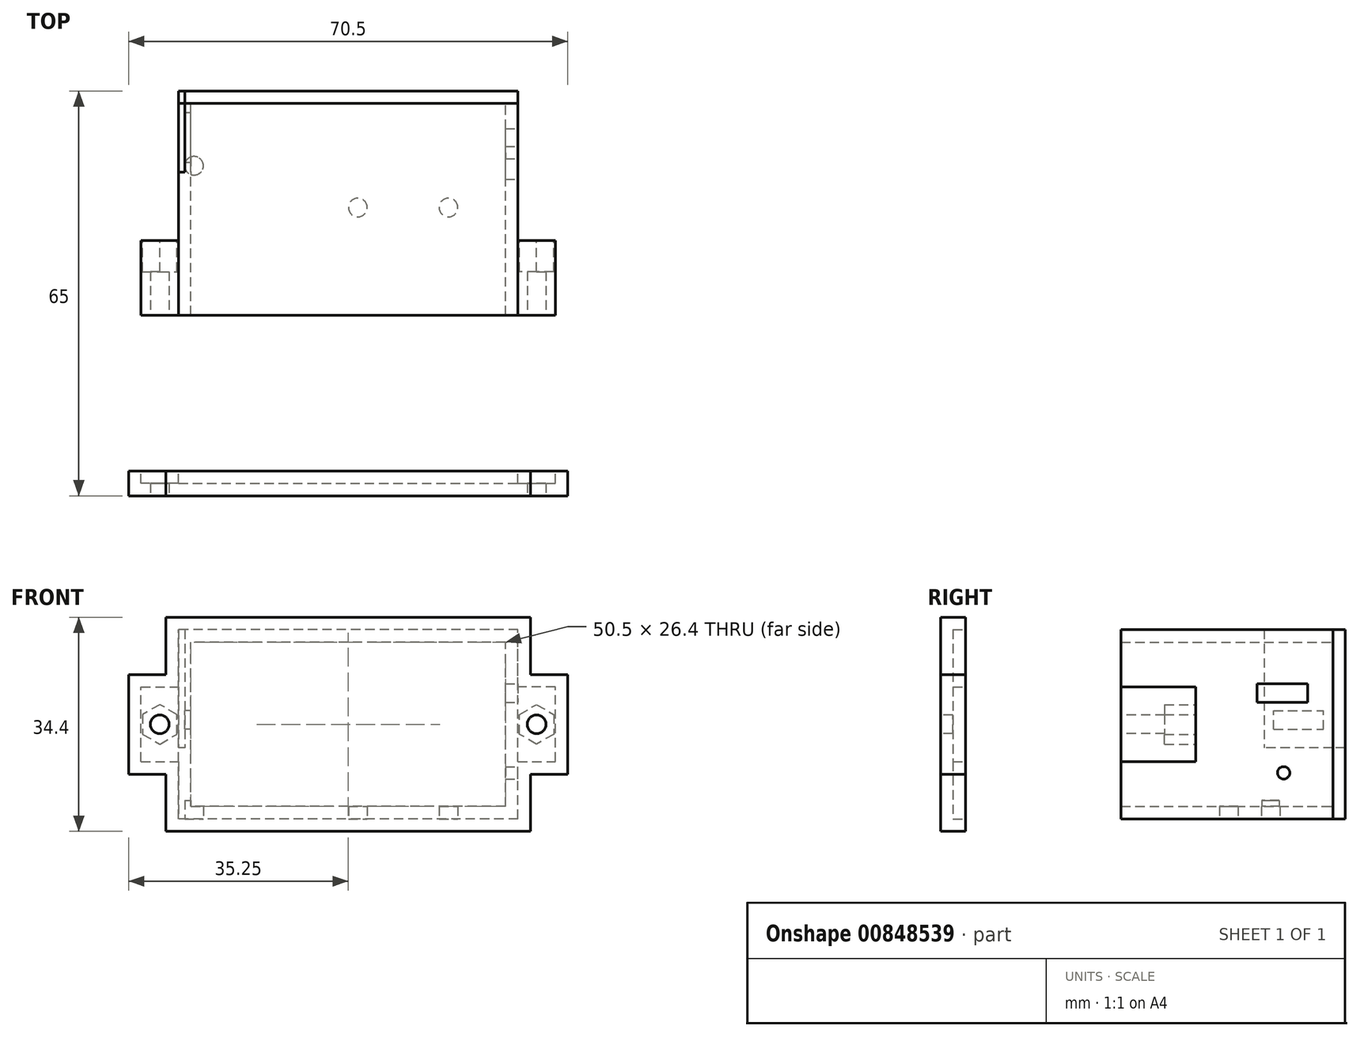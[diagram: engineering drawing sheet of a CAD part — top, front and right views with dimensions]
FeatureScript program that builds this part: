
annotation { "Feature Type Name" : "Feature", "Feature Type Description" : "" }
export const myFeature = defineFeature(function(context is Context, id is Id, definition is map)
    precondition{}
    {
        {
            var Q0;
            Q0=qCreatedBy(makeId("Front.planeOp"),FACE);
            var sketch = newSketch(context, id + "F0", { "sketchPlane" : qUnion([Q0])});
            skLineSegment(sketch, "E0.bottom", {"start": v(27.25, -15.2) * mm, "end": v(-27.25, -15.2) * mm});
            skLineSegment(sketch, "E0.top", {"start": v(27.25, 15.2) * mm, "end": v(-27.25, 15.2) * mm});
            skLineSegment(sketch, "E0.left", {"start": v(27.25, -15.2) * mm, "end": v(27.25, 15.2) * mm});
            skLineSegment(sketch, "E0.right", {"start": v(-27.25, -15.2) * mm, "end": v(-27.25, 15.2) * mm});
            skPoint(sketch, "E0.middle", {"position": v(0, 0) * mm});
            skLineSegment(sketch, "E1.bottom", {"start": v(25.25, -13.2) * mm, "end": v(-25.25, -13.2) * mm});
            skLineSegment(sketch, "E1.top", {"start": v(25.25, 13.2) * mm, "end": v(-25.25, 13.2) * mm});
            skLineSegment(sketch, "E1.left", {"start": v(25.25, -13.2) * mm, "end": v(25.25, 13.2) * mm});
            skLineSegment(sketch, "E1.right", {"start": v(-25.25, -13.2) * mm, "end": v(-25.25, 13.2) * mm});
            skSolve(sketch);
        }
        {
            var Q0;
            Q0=qSketchRegion(id+"F0",true);
            extrude(context, id + "F1", {"entities" : qUnion([Q0]), "depth" : 34 * mm, "offsetDistance" : 25 * mm});
        }
        {
            var Q0;
            Q0=makeQuery(id+"F1.opExtrude","CAP_FACE",FACE,{"disambiguationData":[OSD([sQuery(id+"F0.wireOp",EDGE,"E0.bottom"),sQuery(id+"F0.wireOp",EDGE,"E0.top"),sQuery(id+"F0.wireOp",EDGE,"E0.left"),sQuery(id+"F0.wireOp",EDGE,"E0.right"),sQuery(id+"F0.wireOp",EDGE,"E1.bottom"),sQuery(id+"F0.wireOp",EDGE,"E1.top"),sQuery(id+"F0.wireOp",EDGE,"E1.left"),sQuery(id+"F0.wireOp",EDGE,"E1.right")])],"isStart":true});
            var sketch = newSketch(context, id + "F2", { "sketchPlane" : qUnion([Q0])});
            skLineSegment(sketch, "E2.0.0", {"start": v(-27.25, 15.2) * mm, "end": v(-27.25, -15.2) * mm});
            skLineSegment(sketch, "E2.0.1", {"start": v(-27.25, -15.2) * mm, "end": v(27.25, -15.2) * mm});
            skLineSegment(sketch, "E2.0.2", {"start": v(27.25, -15.2) * mm, "end": v(27.25, 15.2) * mm});
            skLineSegment(sketch, "E2.0.3", {"start": v(27.25, 15.2) * mm, "end": v(-27.25, 15.2) * mm});
            skSolve(sketch);
        }
        {
            var Q0;
            Q0=qSketchRegion(id+"F2",true);
            extrude(context, id + "F3", {"entities" : qUnion([Q0]), "depth" : 2 * mm, "offsetDistance" : 25 * mm});
        }
        {
            var Q0;
            Q0=makeQuery(id+"F1.opExtrude","SWEPT_FACE",FACE,{"disambiguationData":[OSD([sQuery(id+"F0.wireOp",EDGE,"E0.right")])]});
            var sketch = newSketch(context, id + "F4", { "sketchPlane" : qUnion([Q0])});
            skLineSegment(sketch, "E3.bottom", {"start": v(22, -6) * mm, "end": v(34, -6) * mm});
            skLineSegment(sketch, "E3.top", {"start": v(22, 6) * mm, "end": v(34, 6) * mm});
            skLineSegment(sketch, "E3.left", {"start": v(22, -6) * mm, "end": v(22, 6) * mm});
            skLineSegment(sketch, "E3.right", {"start": v(34, -6) * mm, "end": v(34, 6) * mm});
            skPoint(sketch, "E3.middle", {"position": v(28, 0) * mm});
            skPoint(sketch, "E4.orphan", {"position": v(34, 15.2) * mm});
            skPoint(sketch, "E5.orphan", {"position": v(34, -15.2) * mm});
            skSolve(sketch);
        }
        {
            var Q0;
            Q0=qSketchRegion(id+"F4",true);
            extrude(context, id + "F5", {"entities" : qUnion([Q0]), "depth" : 6 * mm, "offsetDistance" : 25 * mm});
        }
        {
            var Q0;
            Q0=makeQuery(id+"F5.opExtrude","SWEPT_FACE",FACE,{"disambiguationData":[OSD([sQuery(id+"F4.wireOp",EDGE,"E3.right")])]});
            var sketch = newSketch(context, id + "F6", { "sketchPlane" : qUnion([Q0])});
            skLineSegment(sketch, "E6.0.0", {"start": v(-27.25, -6) * mm, "end": v(-27.25, 6) * mm, "construction": true});
            skLineSegment(sketch, "E6.0.1", {"start": v(-27.25, 6) * mm, "end": v(-33.25, 6) * mm, "construction": true});
            skLineSegment(sketch, "E6.0.2", {"start": v(-33.25, 6) * mm, "end": v(-33.25, -6) * mm, "construction": true});
            skLineSegment(sketch, "E6.0.3", {"start": v(-33.25, -6) * mm, "end": v(-27.25, -6) * mm, "construction": true});
            skCircle(sketch, "E7", {"center": v(-30.25, 0) * mm, "radius": 1.5 * mm});
            skPoint(sketch, "E7.centerSnap0", {"position": v(-27.25, 0) * mm});
            skSolve(sketch);
        }
        {
            var Q0;
            Q0=qSketchRegion(id+"F6",true);
            extrude(context, id + "F7", {"entities" : qUnion([Q0]), "operationType" : NewBodyOperationType.REMOVE, "oppositeDirection" : true, "depth" : 15 * mm, "offsetDistance" : 25 * mm});
        }
        {
            var Q0;
            Q0=makeQuery(id+"F5.opExtrude","SWEPT_FACE",FACE,{"disambiguationData":[OSD([sQuery(id+"F4.wireOp",EDGE,"E3.left")])]});
            var sketch = newSketch(context, id + "F8", { "sketchPlane" : qUnion([Q0])});
            skCircle(sketch, "E8.0", {"center": v(30.25, 0) * mm, "radius": 1.5 * mm});
            skCircle(sketch, "E9.cCircle", {"center": v(30.25, 0) * mm, "radius": 2.75 * mm, "construction": true});
            skLineSegment(sketch, "E9.0", {"start": v(30.25, -3.18) * mm, "end": v(27.5, -1.59) * mm});
            skLineSegment(sketch, "E9.1", {"start": v(27.5, -1.59) * mm, "end": v(27.5, 1.59) * mm});
            skLineSegment(sketch, "E9.2", {"start": v(27.5, 1.59) * mm, "end": v(30.25, 3.18) * mm});
            skLineSegment(sketch, "E9.3", {"start": v(30.25, 3.18) * mm, "end": v(33, 1.59) * mm});
            skLineSegment(sketch, "E9.4", {"start": v(33, 1.59) * mm, "end": v(33, -1.59) * mm});
            skLineSegment(sketch, "E9.5", {"start": v(33, -1.59) * mm, "end": v(30.25, -3.18) * mm});
            skPoint(sketch, "E9.0.midPoint", {"position": v(28.88, -2.38) * mm});
            skSolve(sketch);
        }
        {
            var Q0;
            Q0=qSketchRegion(id+"F8",true);
            extrude(context, id + "F9", {"entities" : qUnion([Q0]), "operationType" : NewBodyOperationType.REMOVE, "oppositeDirection" : true, "depth" : 5 * mm, "offsetDistance" : 25 * mm});
        }
        {
            var Q0;
            Q0=makeQuery(id+"F5.opExtrude","SWEPT_BODY",BODY,{"disambiguationData":[OSD([sQuery(id+"F4.wireOp",EDGE,"E3.bottom"),sQuery(id+"F4.wireOp",EDGE,"E3.top"),sQuery(id+"F4.wireOp",EDGE,"E3.left"),sQuery(id+"F4.wireOp",EDGE,"E3.right")])]});
            var Q1;
            Q1=qCreatedBy(makeId("Right.planeOp"),FACE);
            mirror(context, id + "F10", {"entities" : qUnion([Q0]), "mirrorPlane" : qUnion([Q1])});
        }
        {
            var Q0;
            Q0=makeQuery(id+"F1.opExtrude","CAP_FACE",FACE,{"disambiguationData":[OSD([sQuery(id+"F0.wireOp",EDGE,"E0.bottom"),sQuery(id+"F0.wireOp",EDGE,"E0.top"),sQuery(id+"F0.wireOp",EDGE,"E0.left"),sQuery(id+"F0.wireOp",EDGE,"E0.right"),sQuery(id+"F0.wireOp",EDGE,"E1.bottom"),sQuery(id+"F0.wireOp",EDGE,"E1.top"),sQuery(id+"F0.wireOp",EDGE,"E1.left"),sQuery(id+"F0.wireOp",EDGE,"E1.right")])],"isStart":false});
            cPlane(context, id + "F11", {"entities" : qUnion([Q0]), "cplaneType" : CPlaneType.OFFSET, "offset" : 25 * mm, "width" : 150 * mm, "height" : 150 * mm});
        }
        {
            var Q0;
            Q0=qCreatedBy(id+"F11.planeOp",FACE);
            var sketch = newSketch(context, id + "F12", { "sketchPlane" : qUnion([Q0])});
            skLineSegment(sketch, "E10.0.0", {"start": v(27.25, -15.2) * mm, "end": v(27.25, -6) * mm});
            skLineSegment(sketch, "E10.0.1", {"start": v(27.25, 15.2) * mm, "end": v(-27.25, 15.2) * mm});
            skLineSegment(sketch, "E10.0.2", {"start": v(-27.25, 15.2) * mm, "end": v(-27.25, 6) * mm});
            skLineSegment(sketch, "E10.0.3", {"start": v(-27.25, -15.2) * mm, "end": v(27.25, -15.2) * mm});
            skLineSegment(sketch, "E11.0.1", {"start": v(-27.25, 6) * mm, "end": v(-33.25, 6) * mm});
            skLineSegment(sketch, "E11.0.2", {"start": v(-33.25, 6) * mm, "end": v(-33.25, -6) * mm});
            skLineSegment(sketch, "E11.0.3", {"start": v(-33.25, -6) * mm, "end": v(-27.25, -6) * mm});
            skLineSegment(sketch, "E12.0.1", {"start": v(27.25, -6) * mm, "end": v(33.25, -6) * mm});
            skLineSegment(sketch, "E12.0.2", {"start": v(33.25, -6) * mm, "end": v(33.25, 6) * mm});
            skLineSegment(sketch, "E12.0.3", {"start": v(33.25, 6) * mm, "end": v(27.25, 6) * mm});
            skLineSegment(sketch, "E13.trimOffspring", {"start": v(-27.25, -6) * mm, "end": v(-27.25, -15.2) * mm});
            skLineSegment(sketch, "E14.trimOffspring", {"start": v(27.25, 6) * mm, "end": v(27.25, 15.2) * mm});
            skSolve(sketch);
        }
        {
            var Q0;
            Q0=qSketchRegion(id+"F12",true);
            extrude(context, id + "F13", {"entities" : qUnion([Q0]), "depth" : 2 * mm, "offsetDistance" : 25 * mm});
        }
        {
            var Q0;
            Q0=makeQuery(id+"F13.opExtrude","CAP_FACE",FACE,{"disambiguationData":[OSD([sQuery(id+"F12.wireOp",EDGE,"E10.0.0"),sQuery(id+"F12.wireOp",EDGE,"E10.0.1"),sQuery(id+"F12.wireOp",EDGE,"E10.0.2"),sQuery(id+"F12.wireOp",EDGE,"E10.0.3"),sQuery(id+"F12.wireOp",EDGE,"E11.0.1"),sQuery(id+"F12.wireOp",EDGE,"E11.0.2"),sQuery(id+"F12.wireOp",EDGE,"E11.0.3"),sQuery(id+"F12.wireOp",EDGE,"E12.0.1"),sQuery(id+"F12.wireOp",EDGE,"E12.0.2"),sQuery(id+"F12.wireOp",EDGE,"E12.0.3"),sQuery(id+"F12.wireOp",EDGE,"64ac5859-c408-4472-a5fe-9f76c2f57aa8.0"),sQuery(id+"F12.wireOp",EDGE,"51b21d13-924f-4e29-874b-db9c67d27de5.0"),sQuery(id+"F12.wireOp",EDGE,"E13.trimOffspring"),sQuery(id+"F12.wireOp",EDGE,"E14.trimOffspring")])],"isStart":true});
            shell(context, id + "F14", {"entities" : qUnion([Q0]), "thickness" : 2 * mm, "oppositeDirection" : true});
        }
        {
            var Q0;
            Q0=makeQuery(id+"F13.opExtrude","CAP_FACE",FACE,{"disambiguationData":[OSD([sQuery(id+"F12.wireOp",EDGE,"E10.0.0"),sQuery(id+"F12.wireOp",EDGE,"E10.0.1"),sQuery(id+"F12.wireOp",EDGE,"E10.0.2"),sQuery(id+"F12.wireOp",EDGE,"E10.0.3"),sQuery(id+"F12.wireOp",EDGE,"E11.0.1"),sQuery(id+"F12.wireOp",EDGE,"E11.0.2"),sQuery(id+"F12.wireOp",EDGE,"E11.0.3"),sQuery(id+"F12.wireOp",EDGE,"E12.0.1"),sQuery(id+"F12.wireOp",EDGE,"E12.0.2"),sQuery(id+"F12.wireOp",EDGE,"E12.0.3"),sQuery(id+"F12.wireOp",EDGE,"E13.trimOffspring"),sQuery(id+"F12.wireOp",EDGE,"E14.trimOffspring")])],"isStart":false});
            var sketch = newSketch(context, id + "F15", { "sketchPlane" : qUnion([Q0])});
            skCircle(sketch, "E15.0", {"center": v(-30.25, 0) * mm, "radius": 1.5 * mm});
            skCircle(sketch, "E16.0", {"center": v(30.25, 0) * mm, "radius": 1.5 * mm});
            skSolve(sketch);
        }
        {
            var Q0;
            Q0=qSketchRegion(id+"F15",true);
            extrude(context, id + "F16", {"entities" : qUnion([Q0]), "operationType" : NewBodyOperationType.REMOVE, "oppositeDirection" : true, "depth" : 3 * mm, "offsetDistance" : 25 * mm});
        }
        {
            var Q0;
            Q0=makeQuery(id+"F1.opExtrude","SWEPT_FACE",FACE,{"disambiguationData":[OSD([sQuery(id+"F0.wireOp",EDGE,"E0.bottom")])]});
            var sketch = newSketch(context, id + "F17", { "sketchPlane" : qUnion([Q0])});
            skLineSegment(sketch, "E17.0.0", {"start": v(-27.25, 0) * mm, "end": v(27.25, 0) * mm, "construction": true});
            skLineSegment(sketch, "E17.0.1", {"start": v(27.25, 0) * mm, "end": v(27.25, 34) * mm, "construction": true});
            skLineSegment(sketch, "E17.0.2", {"start": v(27.25, 34) * mm, "end": v(-27.25, 34) * mm, "construction": true});
            skLineSegment(sketch, "E17.0.3", {"start": v(-27.25, 34) * mm, "end": v(-27.25, 0) * mm, "construction": true});
            skCircle(sketch, "E18", {"center": v(16.1, 16.7) * mm, "radius": 1.5 * mm});
            skCircle(sketch, "E19", {"center": v(1.55, 16.7) * mm, "radius": 1.5 * mm});
            skCircle(sketch, "E20", {"center": v(-24.75, 10) * mm, "radius": 1.5 * mm});
            skSolve(sketch);
        }
        {
            var Q0;
            Q0=qSketchRegion(id+"F17",true);
            extrude(context, id + "F18", {"entities" : qUnion([Q0]), "operationType" : NewBodyOperationType.REMOVE, "oppositeDirection" : true, "depth" : 3 * mm, "offsetDistance" : 25 * mm});
        }
        {
            var Q0;
            Q0=makeQuery(id+"F1.opExtrude","SWEPT_FACE",FACE,{"disambiguationData":[OSD([sQuery(id+"F0.wireOp",EDGE,"E0.right")])]});
            var sketch = newSketch(context, id + "F19", { "sketchPlane" : qUnion([Q0])});
            skLineSegment(sketch, "E21.0.1", {"start": v(0, -15.2) * mm, "end": v(34, -15.2) * mm, "construction": true});
            skLineSegment(sketch, "E21.0.2", {"start": v(34, -15.2) * mm, "end": v(34, 15.2) * mm, "construction": true});
            skLineSegment(sketch, "E21.0.3", {"start": v(34, 15.2) * mm, "end": v(-2, 15.2) * mm, "construction": true});
            skLineSegment(sketch, "E22.bottom", {"start": v(-2, 15.2) * mm, "end": v(11, 15.2) * mm});
            skLineSegment(sketch, "E22.top", {"start": v(-2, -3.8) * mm, "end": v(11, -3.8) * mm});
            skLineSegment(sketch, "E22.left", {"start": v(-2, 15.2) * mm, "end": v(-2, -3.8) * mm});
            skLineSegment(sketch, "E22.right", {"start": v(11, 15.2) * mm, "end": v(11, -3.8) * mm});
            skPoint(sketch, "E23.0", {"position": v(-2, 15.2) * mm});
            skSolve(sketch);
        }
        {
            var Q0;
            Q0=qSketchRegion(id+"F19",true);
            extrude(context, id + "F20", {"entities" : qUnion([Q0]), "operationType" : NewBodyOperationType.REMOVE, "oppositeDirection" : true, "depth" : 1 * mm, "offsetDistance" : 25 * mm});
        }
        {
            var Q0;
            Q0=makeQuery(id+"F1.opExtrude","SWEPT_FACE",FACE,{"disambiguationData":[OSD([sQuery(id+"F0.wireOp",EDGE,"E0.left")])]});
            var sketch = newSketch(context, id + "F21", { "sketchPlane" : qUnion([Q0])});
            skLineSegment(sketch, "E24.0.0", {"start": v(0, -15.2) * mm, "end": v(0, 15.2) * mm});
            skLineSegment(sketch, "E24.0.1", {"start": v(0, 15.2) * mm, "end": v(-34, 15.2) * mm});
            skLineSegment(sketch, "E24.0.2", {"start": v(-34, 15.2) * mm, "end": v(-34, -15.2) * mm});
            skLineSegment(sketch, "E24.0.3", {"start": v(-34, -15.2) * mm, "end": v(0, -15.2) * mm});
            skLineSegment(sketch, "E25.bottom", {"start": v(-4.05, 6.5) * mm, "end": v(-12.15, 6.5) * mm});
            skLineSegment(sketch, "E25.top", {"start": v(-4.05, 3.54) * mm, "end": v(-12.15, 3.54) * mm});
            skLineSegment(sketch, "E25.left", {"start": v(-4.05, 6.5) * mm, "end": v(-4.05, 3.54) * mm});
            skLineSegment(sketch, "E25.right", {"start": v(-12.15, 6.5) * mm, "end": v(-12.15, 3.54) * mm});
            skSolve(sketch);
        }
        {
            var Q0;
            Q0=makeQuery(id+"F21.imprint","IMPRINT",FACE,{"disambiguationData":[TD([[makeQuery(id+"F21.imprint","IMPRINT",EDGE,{"derivedFrom":sQuery(id+"F21.wireOp",EDGE,"E25.bottom")}),1.0]])]});
            var sketch = newSketch(context, id + "F22", { "sketchPlane" : qUnion([Q0])});
            skPoint(sketch, "E26.0", {"position": v(-8.1, 3.54) * mm});
            skPoint(sketch, "E27.0", {"position": v(-4.05, 3.54) * mm});
            skPoint(sketch, "E28.0", {"position": v(-4.05, 6.5) * mm});
            skPoint(sketch, "E29.0", {"position": v(-12.15, 6.5) * mm});
            skPoint(sketch, "E30.0", {"position": v(-12.15, 3.54) * mm});
            skLineSegment(sketch, "E31.0.0", {"start": v(-12.15, 3.54) * mm, "end": v(-4.05, 3.54) * mm});
            skLineSegment(sketch, "E31.0.1", {"start": v(-4.05, 3.54) * mm, "end": v(-4.05, 6.5) * mm});
            skLineSegment(sketch, "E31.0.2", {"start": v(-4.05, 6.5) * mm, "end": v(-12.15, 6.5) * mm});
            skLineSegment(sketch, "E31.0.3", {"start": v(-12.15, 6.5) * mm, "end": v(-12.15, 3.54) * mm});
            skSolve(sketch);
        }
        {
            var Q0;
            Q0 = qSketchRegion(id + "F22", true);
            extrude(context, id + "F23", {"entities" : qUnion([Q0]), "operationType" : NewBodyOperationType.REMOVE, "oppositeDirection" : true, "depth" : 5 * mm, "offsetDistance" : 25 * mm});
        }
        {
            var Q0;
            Q0=makeQuery(id+"F21.imprint","IMPRINT",FACE,{"disambiguationData":[TD([[makeQuery(id+"F21.imprint","IMPRINT",EDGE,{"derivedFrom":sQuery(id+"F21.wireOp",EDGE,"E24.0.0")}),1.0]])]});
            var sketch = newSketch(context, id + "F24", { "sketchPlane" : qUnion([Q0])});
            skCircle(sketch, "E32", {"center": v(-7.89, -7.8) * mm, "radius": 1 * mm});
            skSolve(sketch);
        }
        {
            var Q0;
            Q0 = qSketchRegion(id + "F24", true);
            extrude(context, id + "F25", {"entities" : qUnion([Q0]), "operationType" : NewBodyOperationType.REMOVE, "oppositeDirection" : true, "depth" : 5 * mm, "offsetDistance" : 25 * mm});
        }
        {
            var Q0;
            {var subQ0=sQuery(id+"F0.wireOp",EDGE,"E0.top");var subQ1=sQuery(id+"F19.wireOp",EDGE,"E22.right");var subQ2=sQuery(id+"F19.wireOp",EDGE,"E22.top");Q0=makeQuery(id+"F20.boolean.opBoolean","COPY",FACE,{"disambiguationData":[TD([makeQuery(id+"F1.opExtrude","SWEPT_FACE",FACE,{"disambiguationData":[OSD([subQ0])]})])],"derivedFrom":makeQuery(id+"F20.opExtrude","CAP_FACE",FACE,{"disambiguationData":[OSD([sQuery(id+"F19.wireOp",EDGE,"E22.bottom"),subQ2,sQuery(id+"F19.wireOp",EDGE,"E22.left"),subQ1])],"isStart":false})});}
            var sketch = newSketch(context, id + "F26", { "sketchPlane" : qUnion([Q0])});
            skLineSegment(sketch, "E33.bottom", {"start": v(9.5, -0.8) * mm, "end": v(1.5, -0.8) * mm});
            skLineSegment(sketch, "E33.top", {"start": v(9.5, 2.2) * mm, "end": v(1.5, 2.2) * mm});
            skLineSegment(sketch, "E33.left", {"start": v(9.5, -0.8) * mm, "end": v(9.5, 2.2) * mm});
            skLineSegment(sketch, "E33.right", {"start": v(1.5, -0.8) * mm, "end": v(1.5, 2.2) * mm});
            skSolve(sketch);
        }
        {
            var Q0;
            Q0=makeQuery(id+"F26.imprint","IMPRINT",FACE,{"disambiguationData":[TD([[makeQuery(id+"F26.imprint","IMPRINT",EDGE,{"derivedFrom":sQuery(id+"F26.wireOp",EDGE,"E33.bottom")}),-1.0]])]});
            extrude(context, id + "F27", {"entities" : qUnion([Q0]), "operationType" : NewBodyOperationType.REMOVE, "oppositeDirection" : true, "depth" : 5 * mm, "offsetDistance" : 25 * mm});
        }
    });
